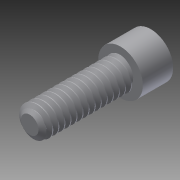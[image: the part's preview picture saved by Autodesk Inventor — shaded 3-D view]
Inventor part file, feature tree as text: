
AUTODESK INVENTOR PART (.ipt)
format: ipt  version: 2015 (Build 190159000, 159)  size: 596,480 bytes
history: native  units: in
note: dims shown in document units (in); Inventor stores cm internally (conversion verified against a paired STEP export)
features: chamfer x1, other x1, extrude x1, imported_body x1, sketch x1, projected_geometry x1
ambient origin geometry x8: Origin, YZ Plane, XZ Plane, XY Plane, X Axis, Y Axis, Z Axis, Center Point
bodies: Body1 (feature_tree)
feature tree (6):
  chamfer  "Chamfer1"  Distance=1.0in
  other  "92185A1341"
  extrude  "Extrusion1"  [1 undecoded]
  imported_body  "Base1"
  sketch  "Sketch1"
  projected_geometry  "Projected Loop1"
note: 1 required parameter value undecoded (feature->parameter linkage not recoverable at this tier; creation-order binding heuristic only, values carry confidence <= 0.55)
